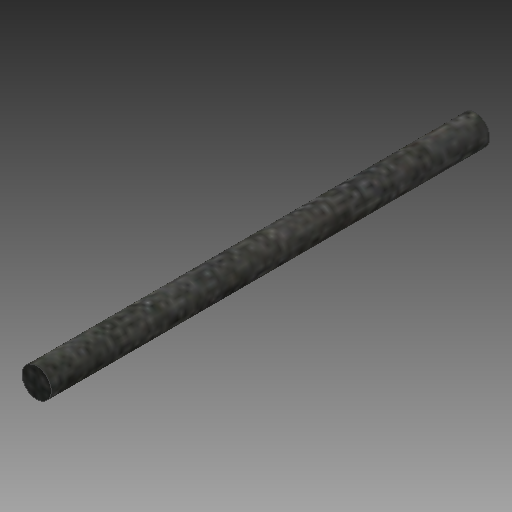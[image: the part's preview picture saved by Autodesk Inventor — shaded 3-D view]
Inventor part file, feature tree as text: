
AUTODESK INVENTOR PART (.ipt)
format: ipt  version: 2018 (Build 220112000, 112)  size: 113,152 bytes
history: native  units: mm
features: other x3, sketch x1
ambient origin geometry x8: Origin, YZ Plane, XZ Plane, XY Plane, X Axis, Y Axis, Z Axis, Center Point
bodies: Volumenkörper1 (feature_tree)
feature tree (4):
  other  "Metall Stab M5_MIR.ipt"
  other  "Volumenkörper1::Metall Stab M5_MIR.ipt"
  other  "Bezeichnung1"
  sketch  "Skizze1"  dims[d0=10.0mm]
